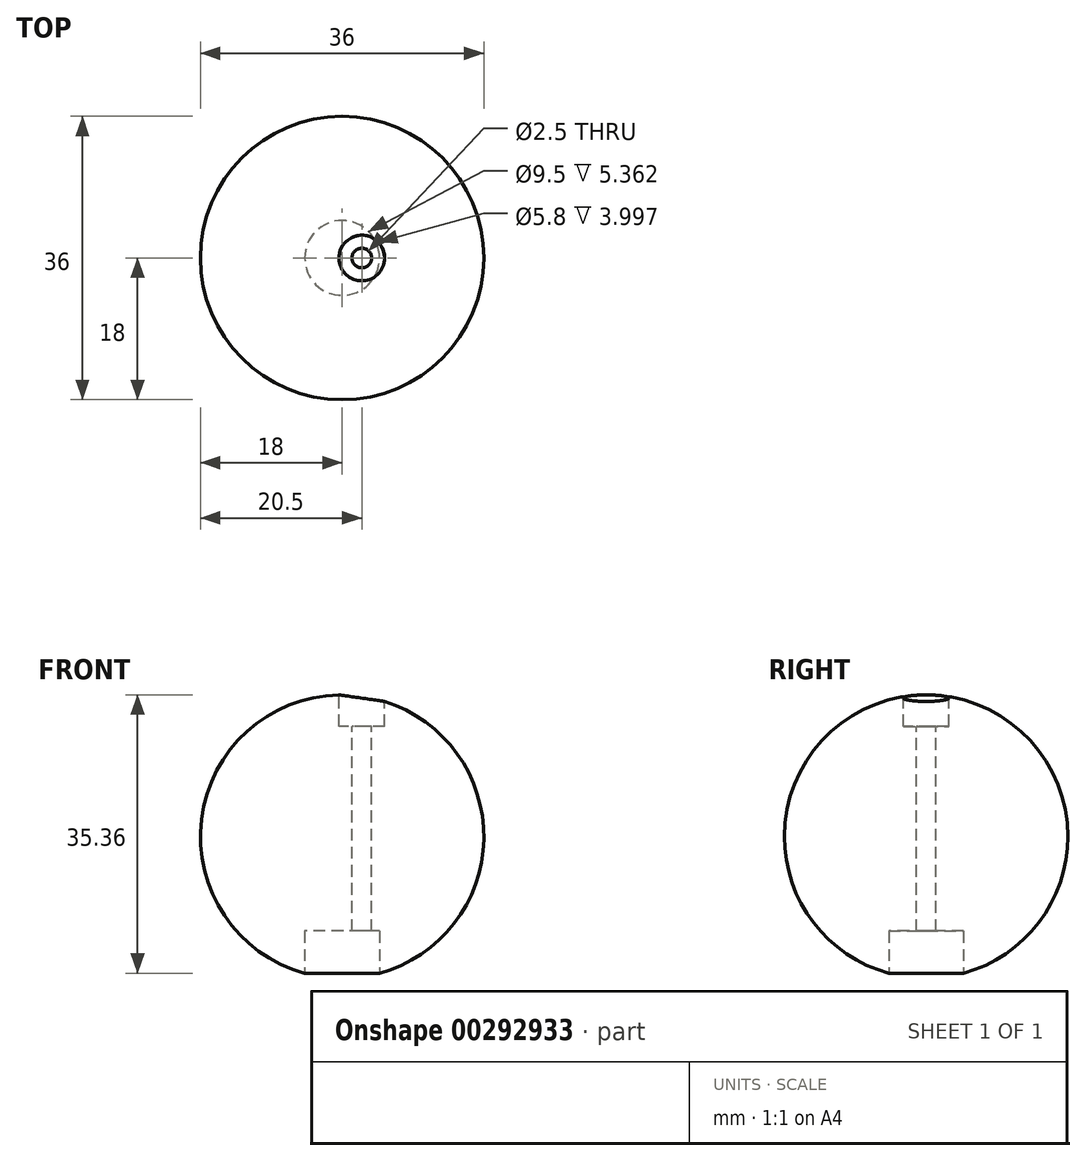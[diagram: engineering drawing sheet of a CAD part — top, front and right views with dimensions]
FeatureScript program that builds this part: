
annotation { "Feature Type Name" : "Feature", "Feature Type Description" : "" }
export const myFeature = defineFeature(function(context is Context, id is Id, definition is map)
    precondition{}
    {
        {
            var Q0;
            Q0=qCreatedBy(makeId("Top.planeOp"),FACE);
            var sketch = newSketch(context, id + "F0", { "sketchPlane" : qUnion([Q0])});
            skArc(sketch, "E0", {"start": v(0, 18) * mm, "mid": v(-18, 0) * mm, "end": v(0, -18) * mm});
            skLineSegment(sketch, "E1", {"start": v(0, 18) * mm, "end": v(0, -18) * mm});
            skSolve(sketch);
        }
        {
            var Q0;
            Q0=qCreatedBy(makeId("Top.planeOp"),FACE);
            var sketch = newSketch(context, id + "F1", { "sketchPlane" : qUnion([Q0])});
            skLineSegment(sketch, "E2", {"start": v(0, 40.82) * mm, "end": v(0, -42.49) * mm, "construction": true});
            skSolve(sketch);
        }
        {
            var Q0;
            Q0 = qSketchRegion(id + "F0", true);
            var Q1;
            Q1=sQuery(id+"F1.wireOp",EDGE,"E2");
            revolve(context, id + "F2", {"entities" : qUnion([Q0]), "axis" : qUnion([Q1]), "revolveType" : RevolveType.FULL});
        }
        {
            var Q0;
            Q0=qCreatedBy(makeId("Top.planeOp"),FACE);
            cPlane(context, id + "F3", {"entities" : qUnion([Q0]), "cplaneType" : CPlaneType.OFFSET, "offset" : 18 * mm, "oppositeDirection" : true, "width" : 150 * mm, "height" : 150 * mm});
        }
        {
            var Q0;
            Q0=qCreatedBy(makeId("Top.planeOp"),FACE);
            cPlane(context, id + "F4", {"entities" : qUnion([Q0]), "cplaneType" : CPlaneType.OFFSET, "offset" : 18 * mm, "width" : 150 * mm, "height" : 150 * mm});
        }
        {
            var Q0;
            Q0=qCreatedBy(makeId("Front.planeOp"),FACE);
            var sketch = newSketch(context, id + "F5", { "sketchPlane" : qUnion([Q0])});
            skLineSegment(sketch, "E3", {"start": v(0, 36.54) * mm, "end": v(0, -38.21) * mm, "construction": true});
            skSolve(sketch);
        }
        {
            var Q0;
            Q0=sQuery(id+"F5.wireOp",EDGE,"E3");
            cPlane(context, id + "F6", {"entities" : qUnion([Q0]), "cplaneType" : CPlaneType.LINE_ANGLE, "offset" : 25 * mm, "angle" : 120 * degree, "width" : 150 * mm, "height" : 150 * mm});
        }
        {
            var Q0;
            Q0=sQuery(id+"F5.wireOp",EDGE,"E3");
            cPlane(context, id + "F7", {"entities" : qUnion([Q0]), "cplaneType" : CPlaneType.LINE_ANGLE, "offset" : 25 * mm, "angle" : 240 * degree, "width" : 150 * mm, "height" : 150 * mm});
        }
        {
            var Q0;
            Q0=qCreatedBy(id+"F4.planeOp",FACE);
            var sketch = newSketch(context, id + "F8", { "sketchPlane" : qUnion([Q0])});
            skCircle(sketch, "E4", {"center": v(2.5, 0) * mm, "radius": 1.25 * mm});
            skSolve(sketch);
        }
        {
            var Q0;
            Q0 = qSketchRegion(id + "F8", true);
            extrude(context, id + "F9", {"entities" : qUnion([Q0]), "operationType" : NewBodyOperationType.REMOVE, "endBound" : BoundingType.THROUGH_ALL, "oppositeDirection" : true, "depth" : 25 * mm});
        }
        {
            var Q0;
            Q0=qCreatedBy(id+"F3.planeOp",FACE);
            var sketch = newSketch(context, id + "F10", { "sketchPlane" : qUnion([Q0])});
            skCircle(sketch, "E5", {"center": v(0, 0) * mm, "radius": 4.75 * mm});
            skCircle(sketch, "E6.0", {"center": v(2.5, 0) * mm, "radius": 1.25 * mm});
            skSolve(sketch);
        }
        {
            var Q0;
            Q0 = qSketchRegion(id + "F10", true);
            extrude(context, id + "F11", {"entities" : qUnion([Q0]), "operationType" : NewBodyOperationType.REMOVE, "depth" : 6 * mm});
        }
        {
            var Q0;
            Q0=makeQuery(id+"F11.boolean.opBoolean","COPY",FACE,{"derivedFrom":makeQuery(id+"F11.opExtrude","CAP_FACE",FACE,{"disambiguationData":[OSD([sQuery(id+"F10.wireOp",EDGE,"E5"),sQuery(id+"F10.wireOp",EDGE,"E6.0")])],"isStart":false})});
            var sketch = newSketch(context, id + "F12", { "sketchPlane" : qUnion([Q0])});
            skArc(sketch, "E7", {"start": v(0.45, 3.72) * mm, "mid": v(-3.75, 0) * mm, "end": v(0.45, -3.72) * mm});
            skArc(sketch, "E8", {"start": v(0.45, 3.72) * mm, "mid": v(-1.75, 0) * mm, "end": v(0.45, -3.72) * mm});
            skSolve(sketch);
        }
        {
            var Q0;
            Q0=qCreatedBy(id+"F4.planeOp",FACE);
            var sketch = newSketch(context, id + "F13", { "sketchPlane" : qUnion([Q0])});
            skPoint(sketch, "E9", {"position": v(2.5, 0) * mm});
            skCircle(sketch, "E10", {"center": v(2.5, 0) * mm, "radius": 2.9 * mm});
            skSolve(sketch);
        }
        {
            var Q0;
            Q0 = qSketchRegion(id + "F13", true);
            extrude(context, id + "F14", {"entities" : qUnion([Q0]), "operationType" : NewBodyOperationType.REMOVE, "oppositeDirection" : true, "depth" : 4 * mm});
        }
    });
